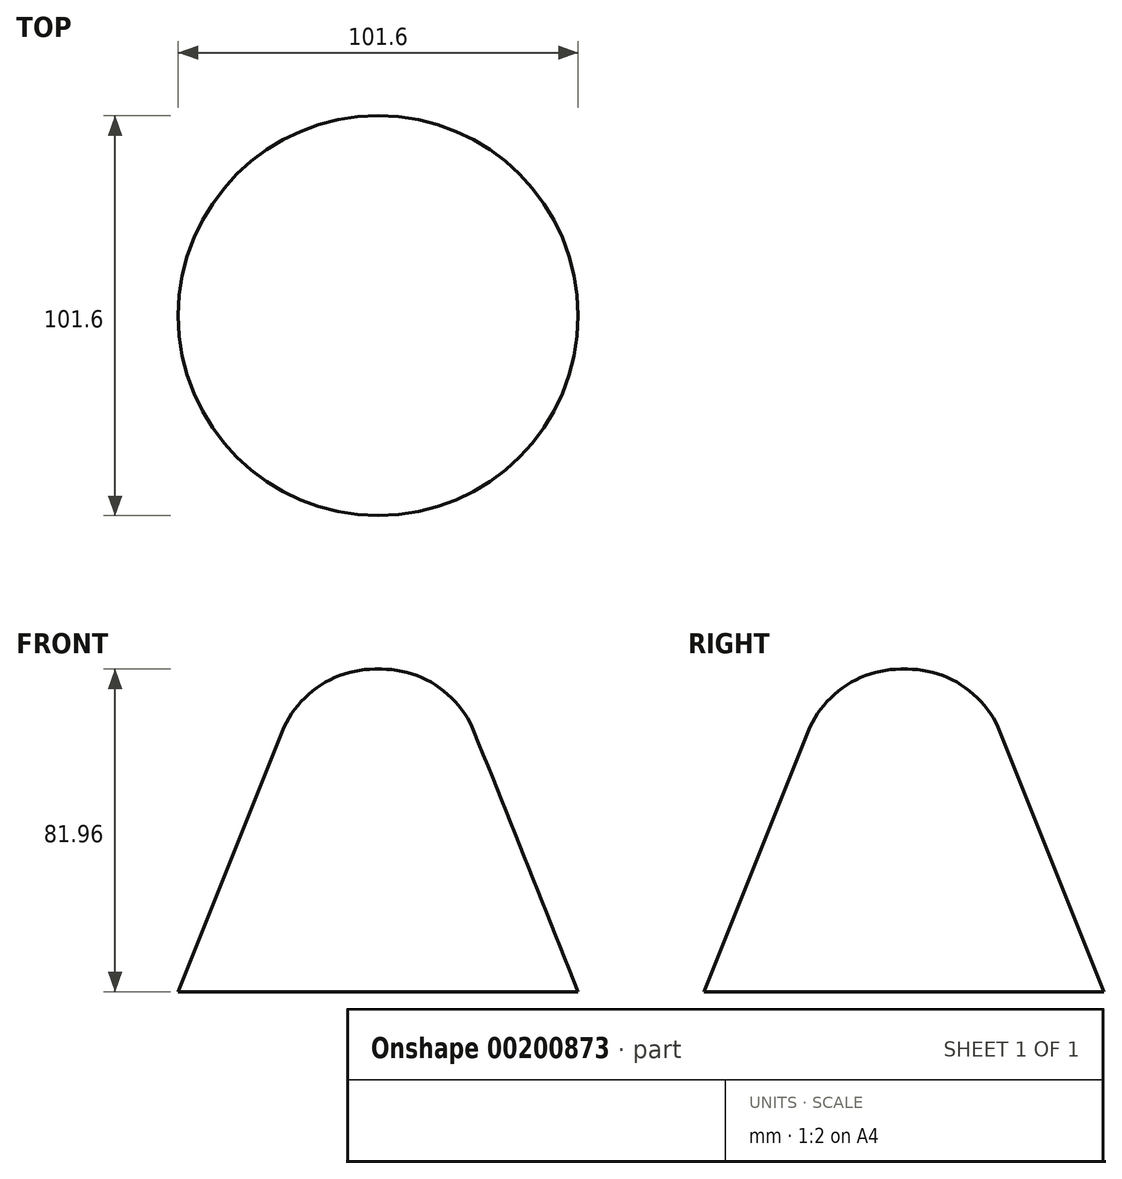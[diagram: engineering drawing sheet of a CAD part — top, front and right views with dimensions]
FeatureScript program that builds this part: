
annotation { "Feature Type Name" : "Feature", "Feature Type Description" : "" }
export const myFeature = defineFeature(function(context is Context, id is Id, definition is map)
    precondition{}
    {
        {
            var Q0;
            Q0=qCreatedBy(makeId("Front.planeOp"),FACE);
            var sketch = newSketch(context, id + "F0", { "sketchPlane" : qUnion([Q0])});
            skLineSegment(sketch, "E0", {"start": v(0, 0) * mm, "end": v(50.8, 0) * mm});
            skLineSegment(sketch, "E1", {"start": v(50.8, 0) * mm, "end": v(0, 127) * mm});
            skLineSegment(sketch, "E2", {"start": v(0, 127) * mm, "end": v(0, 0) * mm});
            skPoint(sketch, "E3", {"position": v(0, 127) * mm});
            skLineSegment(sketch, "E4", {"start": v(18.02, 81.96) * mm, "end": v(0, 81.96) * mm});
            skSolve(sketch);
        }
        {
            var Q0;
            {var subQ0=sQuery(id+"F0.wireOp",EDGE,"E0");Q0=makeQuery(id+"F0.imprint","IMPRINT",FACE,{"disambiguationData":[TD([[makeQuery(id+"F0.imprint","IMPRINT",EDGE,{"derivedFrom":subQ0}),1.0]])]});}
            var Q1;
            Q1=sQuery(id+"F0.wireOp",EDGE,"E2");
            revolve(context, id + "F1", {"entities" : qUnion([Q0]), "axis" : qUnion([Q1]), "revolveType" : RevolveType.FULL});
        }
        {
            var Q0;
            Q0=makeQuery(id+"F1.opRevolve","SWEPT_EDGE",EDGE,{"disambiguationData":[OSD([sQuery(id+"F0.wireOp",EDGE,"E1"),sQuery(id+"F0.wireOp",EDGE,"E4")])]});
            fillet(context, id + "F2", {"entities" : qUnion([Q0]), "radius" : 25.4 * mm, "tangentPropagation" : true, "allowEdgeOverflow" : false});
        }
    });
